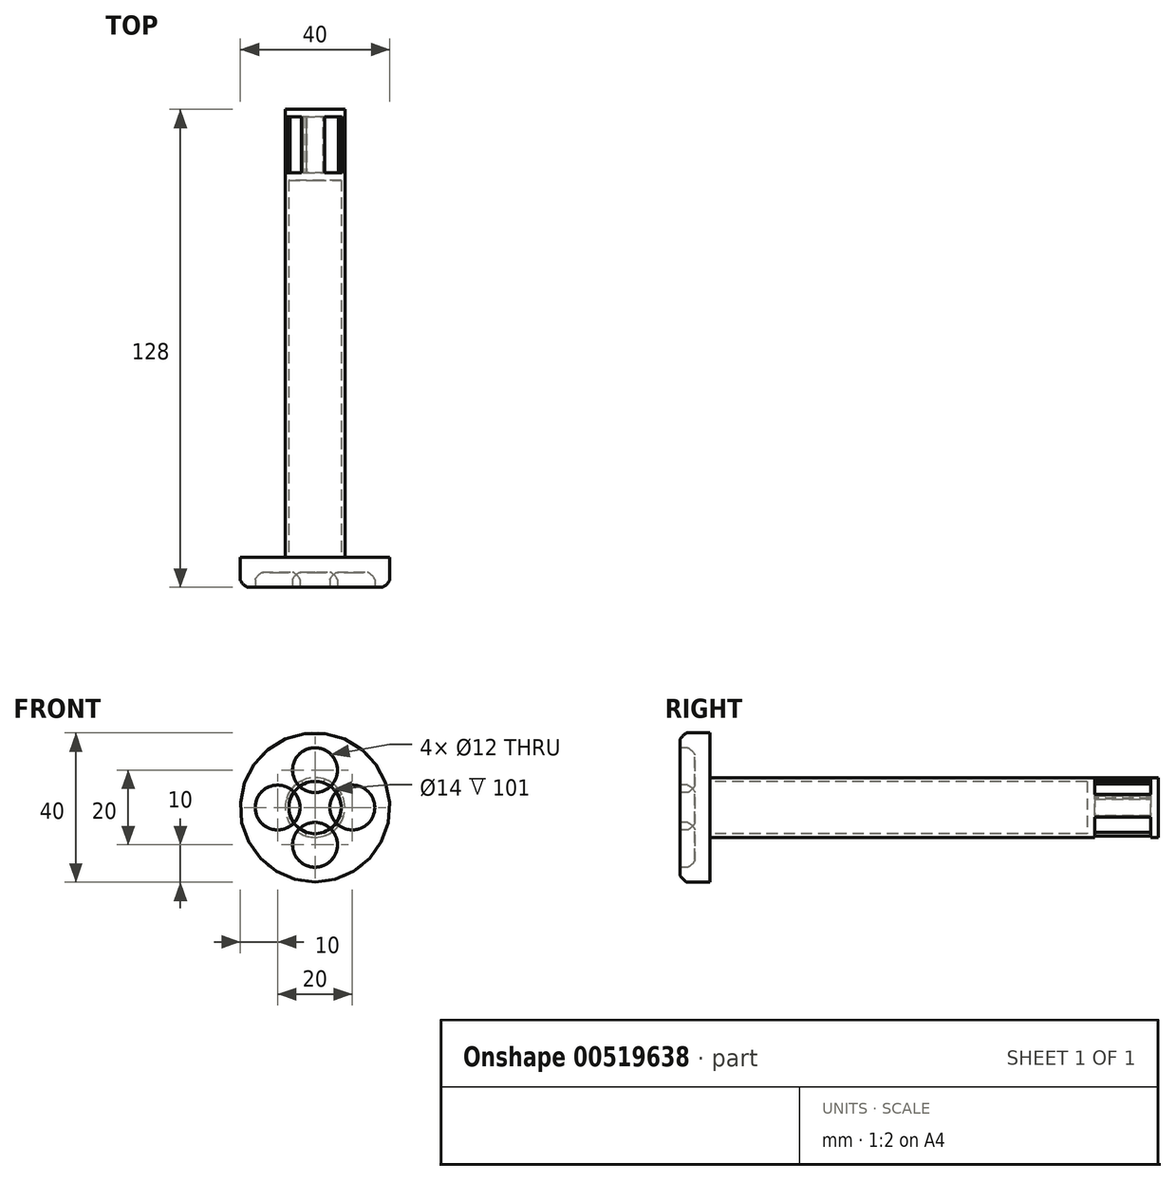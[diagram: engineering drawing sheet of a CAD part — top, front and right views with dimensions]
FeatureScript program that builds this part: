
annotation { "Feature Type Name" : "Feature", "Feature Type Description" : "" }
export const myFeature = defineFeature(function(context is Context, id is Id, definition is map)
    precondition{}
    {
        {
            var Q0;
            Q0=qCreatedBy(makeId("Front.planeOp"),FACE);
            var sketch = newSketch(context, id + "F0", { "sketchPlane" : qUnion([Q0])});
            skCircle(sketch, "E0", {"center": v(0, 0) * mm, "radius": 20 * mm});
            skSolve(sketch);
        }
        {
            var Q0;
            Q0=makeQuery(id+"F0.imprint","IMPRINT",FACE,{"disambiguationData":[TD([[makeQuery(id+"F0.imprint","IMPRINT",EDGE,{"derivedFrom":sQuery(id+"F0.wireOp",EDGE,"E0")}),1.0]])]});
            extrude(context, id + "F1", {"entities" : qUnion([Q0]), "depth" : 8 * mm, "offsetDistance" : 25 * mm});
        }
        {
            var Q0;
            Q0=makeQuery(id+"F1.opExtrude","CAP_FACE",FACE,{"disambiguationData":[OSD([sQuery(id+"F0.wireOp",EDGE,"E0")])],"isStart":false});
            var sketch = newSketch(context, id + "F2", { "sketchPlane" : qUnion([Q0])});
            skLineSegment(sketch, "E1", {"start": v(0, 0) * mm, "end": v(10, 0) * mm});
            skLineSegment(sketch, "E2", {"start": v(0, 0) * mm, "end": v(0, -10) * mm});
            skLineSegment(sketch, "E3", {"start": v(0, 0) * mm, "end": v(0, 10) * mm});
            skLineSegment(sketch, "E4", {"start": v(0, 0) * mm, "end": v(-10, 0) * mm});
            skCircle(sketch, "E5", {"center": v(10, 0) * mm, "radius": 6 * mm});
            skPoint(sketch, "E6.center", {"position": v(0, 0) * mm});
            skCircle(sketch, "E7.1.0", {"center": v(0, -10) * mm, "radius": 6 * mm});
            skCircle(sketch, "E7.2.0", {"center": v(-10, 0) * mm, "radius": 6 * mm});
            skCircle(sketch, "E7.3.0", {"center": v(0, 10) * mm, "radius": 6 * mm});
            skLineSegment(sketch, "E7.anchor1", {"start": v(0, 0) * mm, "end": v(10, 0) * mm, "construction": true});
            skLineSegment(sketch, "E7.anchor2", {"start": v(0, 0) * mm, "end": v(0, 10) * mm, "construction": true});
            skSolve(sketch);
        }
        {
            var Q0;
            Q0=makeQuery(id+"F2.imprint","IMPRINT",FACE,{"disambiguationData":[TD([[makeQuery(id+"F2.imprint","IMPRINT",EDGE,{"derivedFrom":sQuery(id+"F2.wireOp",EDGE,"E5")}),1.0]])]});
            var Q1;
            Q1=makeQuery(id+"F2.imprint","IMPRINT",FACE,{"disambiguationData":[TD([[makeQuery(id+"F2.imprint","IMPRINT",EDGE,{"derivedFrom":sQuery(id+"F2.wireOp",EDGE,"E7.3.0")}),1.0]])]});
            var Q2;
            Q2=makeQuery(id+"F2.imprint","IMPRINT",FACE,{"disambiguationData":[TD([[makeQuery(id+"F2.imprint","IMPRINT",EDGE,{"derivedFrom":sQuery(id+"F2.wireOp",EDGE,"E7.2.0")}),1.0]])]});
            var Q3;
            Q3=makeQuery(id+"F2.imprint","IMPRINT",FACE,{"disambiguationData":[TD([[makeQuery(id+"F2.imprint","IMPRINT",EDGE,{"derivedFrom":sQuery(id+"F2.wireOp",EDGE,"E7.1.0")}),1.0]])]});
            extrude(context, id + "F3", {"entities" : qUnion([Q0, Q1, Q2, Q3]), "operationType" : NewBodyOperationType.REMOVE, "oppositeDirection" : true, "depth" : 4 * mm, "offsetDistance" : 25 * mm});
        }
        {
            var Q0;
            Q0=makeQuery(id+"F3.boolean.opBoolean","COPY",EDGE,{"derivedFrom":makeQuery(id+"F3.opExtrude","CAP_EDGE",EDGE,{"disambiguationData":[OSD([sQuery(id+"F2.wireOp",EDGE,"E7.3.0")])],"isStart":true})});
            var Q1;
            Q1=makeQuery(id+"F3.boolean.opBoolean","COPY",EDGE,{"derivedFrom":makeQuery(id+"F3.opExtrude","CAP_EDGE",EDGE,{"disambiguationData":[OSD([sQuery(id+"F2.wireOp",EDGE,"E7.2.0")])],"isStart":true})});
            var Q2;
            Q2=makeQuery(id+"F3.boolean.opBoolean","COPY",EDGE,{"derivedFrom":makeQuery(id+"F3.opExtrude","CAP_EDGE",EDGE,{"disambiguationData":[OSD([sQuery(id+"F2.wireOp",EDGE,"E7.1.0")])],"isStart":true})});
            var Q3;
            Q3=makeQuery(id+"F3.boolean.opBoolean","COPY",EDGE,{"derivedFrom":makeQuery(id+"F3.opExtrude","CAP_EDGE",EDGE,{"disambiguationData":[OSD([sQuery(id+"F2.wireOp",EDGE,"E5")])],"isStart":true})});
            var Q4;
            Q4=makeQuery(id+"F1.opExtrude","CAP_EDGE",EDGE,{"disambiguationData":[OSD([sQuery(id+"F0.wireOp",EDGE,"E0")])],"isStart":false});
            var Q5;
            Q5=makeQuery(id+"F3.boolean.opBoolean","COPY",EDGE,{"derivedFrom":makeQuery(id+"F3.opExtrude","CAP_EDGE",EDGE,{"disambiguationData":[OSD([sQuery(id+"F2.wireOp",EDGE,"E7.2.0")])],"isStart":false})});
            var Q6;
            Q6=makeQuery(id+"F3.boolean.opBoolean","COPY",EDGE,{"derivedFrom":makeQuery(id+"F3.opExtrude","CAP_EDGE",EDGE,{"disambiguationData":[OSD([sQuery(id+"F2.wireOp",EDGE,"E7.3.0")])],"isStart":false})});
            var Q7;
            Q7=makeQuery(id+"F3.boolean.opBoolean","COPY",EDGE,{"derivedFrom":makeQuery(id+"F3.opExtrude","CAP_EDGE",EDGE,{"disambiguationData":[OSD([sQuery(id+"F2.wireOp",EDGE,"E5")])],"isStart":false})});
            var Q8;
            Q8=makeQuery(id+"F3.boolean.opBoolean","COPY",EDGE,{"derivedFrom":makeQuery(id+"F3.opExtrude","CAP_EDGE",EDGE,{"disambiguationData":[OSD([sQuery(id+"F2.wireOp",EDGE,"E7.1.0")])],"isStart":false})});
            fillet(context, id + "F4", {"entities" : qUnion([Q0, Q1, Q2, Q3, Q4, Q5, Q6, Q7, Q8]), "radius" : 2 * mm, "tangentPropagation" : true, "rho" : 0.2, "crossSection" : FilletCrossSection.CONIC, "allowEdgeOverflow" : false});
        }
        {
            var Q0;
            Q0=makeQuery(id+"F1.opExtrude","CAP_FACE",FACE,{"disambiguationData":[OSD([sQuery(id+"F0.wireOp",EDGE,"E0")])],"isStart":true});
            var sketch = newSketch(context, id + "F5", { "sketchPlane" : qUnion([Q0])});
            skCircle(sketch, "E8", {"center": v(0, 0) * mm, "radius": 7 * mm});
            skCircle(sketch, "E9", {"center": v(0, 0) * mm, "radius": 8 * mm});
            skSolve(sketch);
        }
        {
            var Q0;
            Q0 = qSketchRegion(id + "F5", true);
            extrude(context, id + "F6", {"entities" : qUnion([Q0]), "operationType" : NewBodyOperationType.ADD, "depth" : 120 * mm, "offsetDistance" : 25 * mm});
        }
        {
            var Q0;
            Q0=makeQuery(id+"F6.opExtrude","CAP_FACE",FACE,{"disambiguationData":[OSD([sQuery(id+"F5.wireOp",EDGE,"E8"),sQuery(id+"F5.wireOp",EDGE,"E9")])],"isStart":false});
            var sketch = newSketch(context, id + "F7", { "sketchPlane" : qUnion([Q0])});
            skPoint(sketch, "E10", {"position": v(0, 7) * mm});
            skLineSegment(sketch, "E11", {"start": v(-3.5, 3.5) * mm, "end": v(0, 7) * mm, "construction": true});
            skPoint(sketch, "E12", {"position": v(-1.75, 5.25) * mm});
            skLineSegment(sketch, "E13", {"start": v(0, 0) * mm, "end": v(-1.75, 5.25) * mm, "construction": true});
            skLineSegment(sketch, "E14", {"start": v(-1.75, 5.25) * mm, "end": v(-2.21, 6.64) * mm, "construction": true});
            skPoint(sketch, "E15", {"position": v(-2.21, 6.64) * mm});
            skPoint(sketch, "E16.1.0", {"position": v(-6.26, 3.13) * mm});
            skPoint(sketch, "E16.2.0", {"position": v(-6.64, -2.21) * mm});
            skPoint(sketch, "E16.3.0", {"position": v(-3.13, -6.26) * mm});
            skPoint(sketch, "E16.4.0", {"position": v(2.21, -6.64) * mm});
            skPoint(sketch, "E16.5.0", {"position": v(6.26, -3.13) * mm});
            skPoint(sketch, "E16.6.0", {"position": v(6.64, 2.21) * mm});
            skPoint(sketch, "E16.7.0", {"position": v(3.13, 6.26) * mm});
            skPoint(sketch, "E16.center", {"position": v(0, 0) * mm});
            skLineSegment(sketch, "E17", {"start": v(-6.26, 3.13) * mm, "end": v(-2.21, 6.64) * mm});
            skLineSegment(sketch, "E18", {"start": v(-6.64, -2.21) * mm, "end": v(2.21, -6.64) * mm});
            skLineSegment(sketch, "E19", {"start": v(6.64, 2.21) * mm, "end": v(3.13, 6.26) * mm});
            skLineSegment(sketch, "E20", {"start": v(0, 0) * mm, "end": v(-6.26, 3.13) * mm, "construction": true});
            skLineSegment(sketch, "E21", {"start": v(-6.26, 3.13) * mm, "end": v(-8.94, 4.47) * mm});
            skLineSegment(sketch, "E22", {"start": v(-2.21, 6.64) * mm, "end": v(-3.16, 9.49) * mm});
            skLineSegment(sketch, "E23", {"start": v(0, 0) * mm, "end": v(3.13, 6.26) * mm, "construction": true});
            skLineSegment(sketch, "E24", {"start": v(3.13, 6.26) * mm, "end": v(4.47, 8.94) * mm});
            skLineSegment(sketch, "E25", {"start": v(0, 0) * mm, "end": v(6.64, 2.21) * mm, "construction": true});
            skLineSegment(sketch, "E26", {"start": v(6.64, 2.21) * mm, "end": v(9.49, 3.16) * mm});
            skLineSegment(sketch, "E27", {"start": v(0, 0) * mm, "end": v(2.21, -6.64) * mm, "construction": true});
            skLineSegment(sketch, "E28", {"start": v(2.21, -6.64) * mm, "end": v(3.04, -9.52) * mm});
            skLineSegment(sketch, "E29", {"start": v(0, 0) * mm, "end": v(-6.64, -2.21) * mm, "construction": true});
            skLineSegment(sketch, "E30", {"start": v(-6.64, -2.21) * mm, "end": v(-9.64, -3.21) * mm});
            skLineSegment(sketch, "E31", {"start": v(-8.94, 4.47) * mm, "end": v(-3.16, 9.49) * mm});
            skLineSegment(sketch, "E32", {"start": v(4.47, 8.94) * mm, "end": v(9.49, 3.16) * mm});
            skLineSegment(sketch, "E33", {"start": v(3.04, -9.52) * mm, "end": v(-5.85, -8.3) * mm});
            skLineSegment(sketch, "E34", {"start": v(-5.85, -8.3) * mm, "end": v(-9.64, -3.21) * mm});
            skSolve(sketch);
        }
        {
            var Q0;
            Q0=makeQuery(id+"F6.opExtrude","CAP_FACE",FACE,{"disambiguationData":[OSD([sQuery(id+"F5.wireOp",EDGE,"E8"),sQuery(id+"F5.wireOp",EDGE,"E9")])],"isStart":false});
            var sketch = newSketch(context, id + "F8", { "sketchPlane" : qUnion([Q0])});
            skPoint(sketch, "E35", {"position": v(-1.75, 5.25) * mm});
            skLineSegment(sketch, "E36", {"start": v(0, 0) * mm, "end": v(-1.75, 5.25) * mm});
            skLineSegment(sketch, "E37", {"start": v(-1.75, 5.25) * mm, "end": v(-2.21, 6.64) * mm});
            skSolve(sketch);
        }
        {
            var Q0;
            Q0 = qSketchRegion(id + "F7", true);
            extrude(context, id + "F9", {"entities" : qUnion([Q0]), "operationType" : NewBodyOperationType.REMOVE, "oppositeDirection" : true, "depth" : 17 * mm, "offsetDistance" : 25 * mm});
        }
        {
            var Q0;
            Q0=makeQuery(id+"F9.boolean.opBoolean","COPY",FACE,{"derivedFrom":makeQuery(id+"F9.opExtrude","CAP_FACE",FACE,{"disambiguationData":[OSD([sQuery(id+"F7.wireOp",EDGE,"E18"),sQuery(id+"F7.wireOp",EDGE,"E28"),sQuery(id+"F7.wireOp",EDGE,"E30"),sQuery(id+"F7.wireOp",EDGE,"E33"),sQuery(id+"F7.wireOp",EDGE,"E34")])],"isStart":false})});
            var sketch = newSketch(context, id + "F10", { "sketchPlane" : qUnion([Q0])});
            skCircle(sketch, "E38", {"center": v(0, 0) * mm, "radius": 8 * mm});
            skSolve(sketch);
        }
        {
            var Q0;
            Q0 = qSketchRegion(id + "F10", true);
            extrude(context, id + "F11", {"entities" : qUnion([Q0]), "operationType" : NewBodyOperationType.ADD, "oppositeDirection" : true, "depth" : 2 * mm, "offsetDistance" : 25 * mm});
        }
        {
            var Q0;
            Q0=makeQuery(id+"F8.imprint","IMPRINT",FACE,{"disambiguationData":[TD([[makeQuery(id+"F8.imprint","IMPRINT",EDGE,{"derivedFrom":makeQuery(id+"F6.opExtrude","CAP_EDGE",EDGE,{"disambiguationData":[OSD([sQuery(id+"F5.wireOp",EDGE,"E8")])],"isStart":false})}),-1.0]])]});
            var sketch = newSketch(context, id + "F12", { "sketchPlane" : qUnion([Q0])});
            skCircle(sketch, "E39", {"center": v(0, 0) * mm, "radius": 8 * mm});
            skSolve(sketch);
        }
        {
            var Q0;
            Q0 = qSketchRegion(id + "F12", true);
            extrude(context, id + "F13", {"entities" : qUnion([Q0]), "operationType" : NewBodyOperationType.ADD, "oppositeDirection" : true, "depth" : 2 * mm, "offsetDistance" : 25 * mm});
        }
    });
